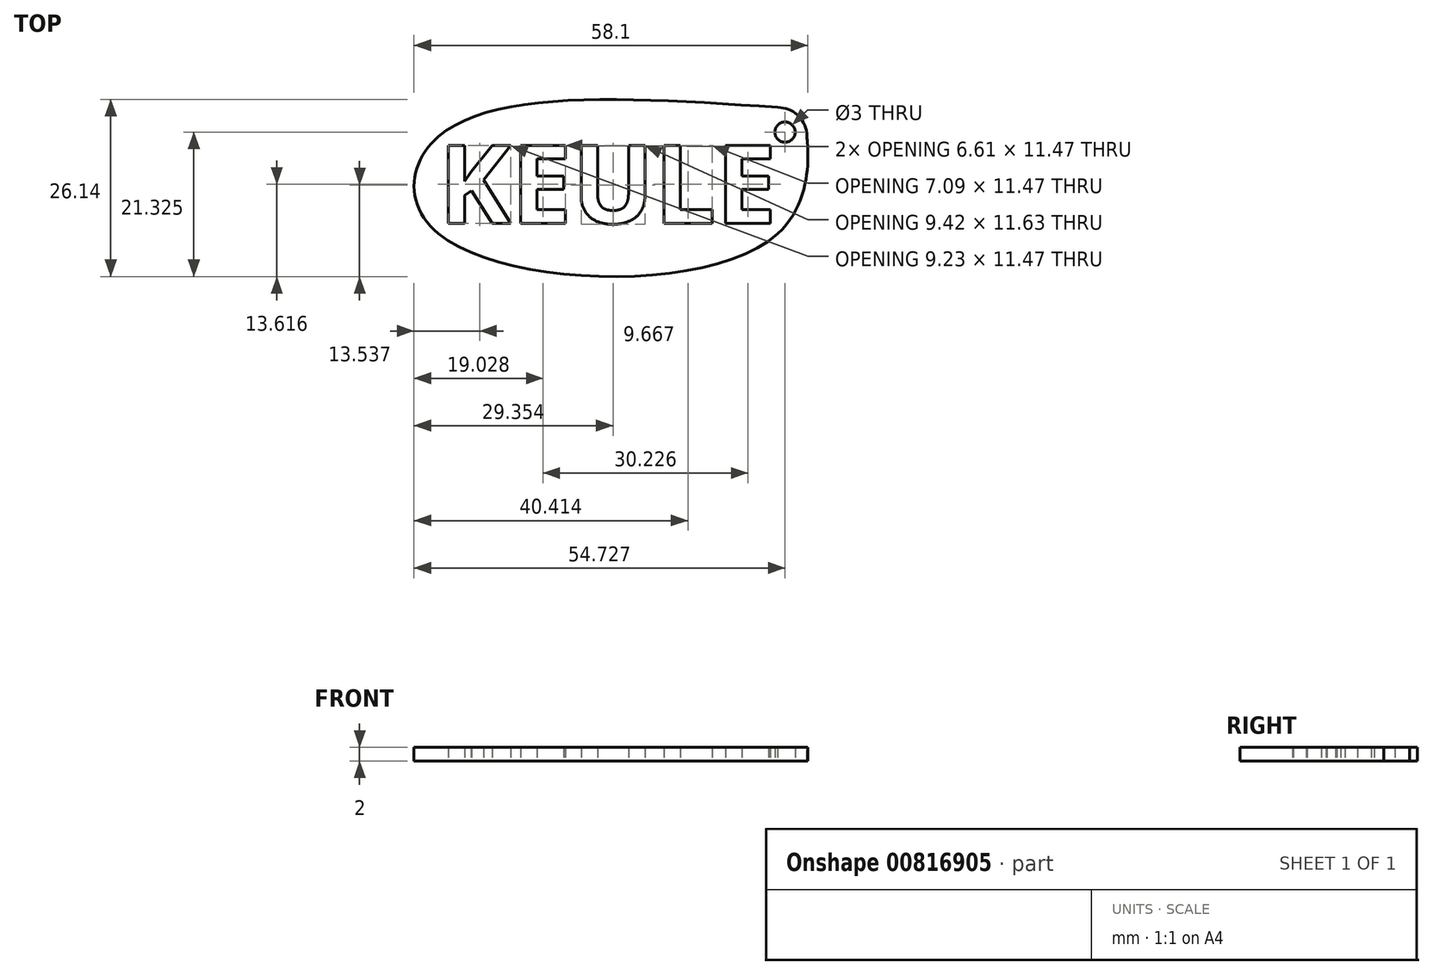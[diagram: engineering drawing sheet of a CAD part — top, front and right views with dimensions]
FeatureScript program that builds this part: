
annotation { "Feature Type Name" : "Feature", "Feature Type Description" : "" }
export const myFeature = defineFeature(function(context is Context, id is Id, definition is map)
    precondition{}
    {
        {
            var Q0;
            Q0=qCreatedBy(makeId("Top.planeOp"),FACE);
            var sketch = newSketch(context, id + "F0", { "sketchPlane" : qUnion([Q0])});
            skText(sketch, "E0", { "text": "KEULE", "fontName": "OpenSans-Bold.ttf"});
            skLineSegment(sketch, "E1.bottom", {"start": v(-25, 12.8) * mm, "end": v(25.04, 12.8) * mm});
            skLineSegment(sketch, "E1.top", {"start": v(-25, -1.56) * mm, "end": v(25.04, -1.56) * mm});
            skLineSegment(sketch, "E1.left", {"start": v(-25, 12.8) * mm, "end": v(-25, -1.56) * mm});
            skLineSegment(sketch, "E1.right", {"start": v(25.04, 12.8) * mm, "end": v(25.04, -1.56) * mm});
            skCircle(sketch, "E2", {"center": v(25.04, 12.8) * mm, "radius": 4.3 * mm});
            skFitSpline(sketch, "E3", {"points": [v(25.04, 17.1) * mm, v(-25, 12.8) * mm, v(-25, -1.56) * mm, v(25.04, -1.56) * mm, v(29.34, 12.8) * mm, v(29.31, 13.3) * mm], "startDerivative": vector(-199.32, 13.57) * mm, "endDerivative": vector(-0.27, 9.4) * mm});
            skCircle(sketch, "E4", {"center": v(26.12, 13.45) * mm, "radius": 1.5 * mm});
            const initialGuessF0  = {"E0": [-0.025, 0, 1, 0, 0.01157]};
            skSetInitialGuess(sketch, initialGuessF0);
            skSolve(sketch);
        }
        {
            var Q0;
            {var subQ0=sQuery(id+"F0.wireOp",EDGE,"E3");var subQ3=sQuery(id+"F0.wireOp",EDGE,"E2");var subQ5=makeQuery(id+"F0.imprint","INTERSECT",VERTEX,{"disambiguationData":[OD(0.0)],"derivedFrom":[subQ3,subQ0]});Q0=makeQuery(id+"F0.imprint","IMPRINT",FACE,{"disambiguationData":[TD([[makeQuery(id+"F0.imprint","IMPRINT",EDGE,{"disambiguationData":[TD([[subQ5,-1.0]])],"derivedFrom":subQ3}),-1.0]])]});}
            var Q1;
            Q1=makeQuery(id+"F0.imprint","IMPRINT",FACE,{"disambiguationData":[TD([[makeQuery(id+"F0.imprint","IMPRINT",EDGE,{"derivedFrom":sQuery(id+"F0.wireOp",EDGE,"E0.sketch_text.stroke-0")}),1.0]])]});
            var Q2;
            {var subQ0=sQuery(id+"F0.wireOp",EDGE,"E1.top");Q2=makeQuery(id+"F0.imprint","IMPRINT",FACE,{"disambiguationData":[TD([[makeQuery(id+"F0.imprint","IMPRINT",EDGE,{"derivedFrom":subQ0}),-1.0]])]});}
            var Q3;
            {var subQ0=sQuery(id+"F0.wireOp",EDGE,"E1.left");Q3=makeQuery(id+"F0.imprint","IMPRINT",FACE,{"disambiguationData":[TD([[makeQuery(id+"F0.imprint","IMPRINT",EDGE,{"derivedFrom":subQ0}),-1.0]])]});}
            var Q4;
            {var subQ0=sQuery(id+"F0.wireOp",EDGE,"E3");var subQ3=sQuery(id+"F0.wireOp",EDGE,"E2");var subQ5=makeQuery(id+"F0.imprint","INTERSECT",VERTEX,{"disambiguationData":[OD(2.0)],"derivedFrom":[subQ3,subQ0]});Q4=makeQuery(id+"F0.imprint","IMPRINT",FACE,{"disambiguationData":[TD([[makeQuery(id+"F0.imprint","IMPRINT",EDGE,{"disambiguationData":[TD([[subQ5,1.0]])],"derivedFrom":subQ3}),-1.0]])]});}
            var Q5;
            {var subQ1=sQuery(id+"F0.wireOp",EDGE,"E2");var subQ3=sQuery(id+"F0.wireOp",EDGE,"E1.bottom");var subQ4=makeQuery(id+"F0.imprint","INTERSECT",VERTEX,{"derivedFrom":[subQ3,subQ1]});Q5=makeQuery(id+"F0.imprint","IMPRINT",FACE,{"disambiguationData":[TD([[makeQuery(id+"F0.imprint","IMPRINT",EDGE,{"disambiguationData":[TD([[subQ4,-1.0]])],"derivedFrom":subQ3}),1.0]])]});}
            var Q6;
            {var subQ5=sQuery(id+"F0.wireOp",EDGE,"E0.sketch_text.stroke-49");Q6=makeQuery(id+"F0.imprint","IMPRINT",FACE,{"disambiguationData":[TD([[makeQuery(id+"F0.imprint","IMPRINT",EDGE,{"derivedFrom":subQ5}),1.0]])]});}
            extrude(context, id + "F1", {"entities" : qUnion([Q0, Q1, Q2, Q3, Q4, Q5, Q6]), "depth" : 2 * mm, "offsetDistance" : 25 * mm});
        }
    });
